# Revit family: EstaciondeLavado_Autocontenida_MueblePiso_Corona
name_source: partatom
category: Plumbing Fixtures
units: mm (PartAtom-declared; Revit-internal decimal feet)

## family parameters
Always vertical = Yes
Cut with Voids When Loaded = No
Host = Floor
OmniClass Number = 23.31.25.13
OmniClass Title = Bathroom Cabinets
Part Type = Normal
Room Calculation Point = No
Round Connector Dimension = Use Diameter
Shared = No

## types (1)
- EstaciondeLavado_Autocontenida_MueblePiso_Corona
    Alto = 1160 mm  [stored 3.80577 ft]
    Ancho = 450 mm  [stored 1.47638 ft]
    Creado por = BIMBAU
    Default Elevation = 0 mm  [stored 0 ft]
    Description = La Estación de lavado autocontenida piso cumple con todos los protocolos de seguridad que te ayudarán a velar por el bienestar de tu personal; además, incluye las tecnologías CoverGloss y AquaFlow. Es totalmente la solución práctica, compacta y segura para tu empresa, ya que cuenta con accionamiento seguro y sin contacto.
    Fecha de creación = 12/03/2021
    Forma = Cuadrado
    Manufacturer = Corona
    Material = Corona_Porcelana_Sanitaria
    Material 2 = Corona_Plastico_Negro
    Model = Estacion de Lavado Autocontenida Mueble Piso
    Peso  Bruto = 8.8 kg (19.4 lb)
    Peso neto = 8 kg (17.6 lb)
    Profundidad = 450 mm  [stored 1.47638 ft]
    Referencia = O60491001
    Tipo de instalación = Sobrepuesto en mueble (85 cm - 33 7/16” desde el piso)
    Tipo de lavamanos = De mesón integrado

note: [stored X ft] marks values corroborated as IEEE doubles in the binary element streams (Revit-internal decimal feet)

## geometry (parser evidence)
native form markers: Sweep x4
no freeform markers — native parametric forms only
